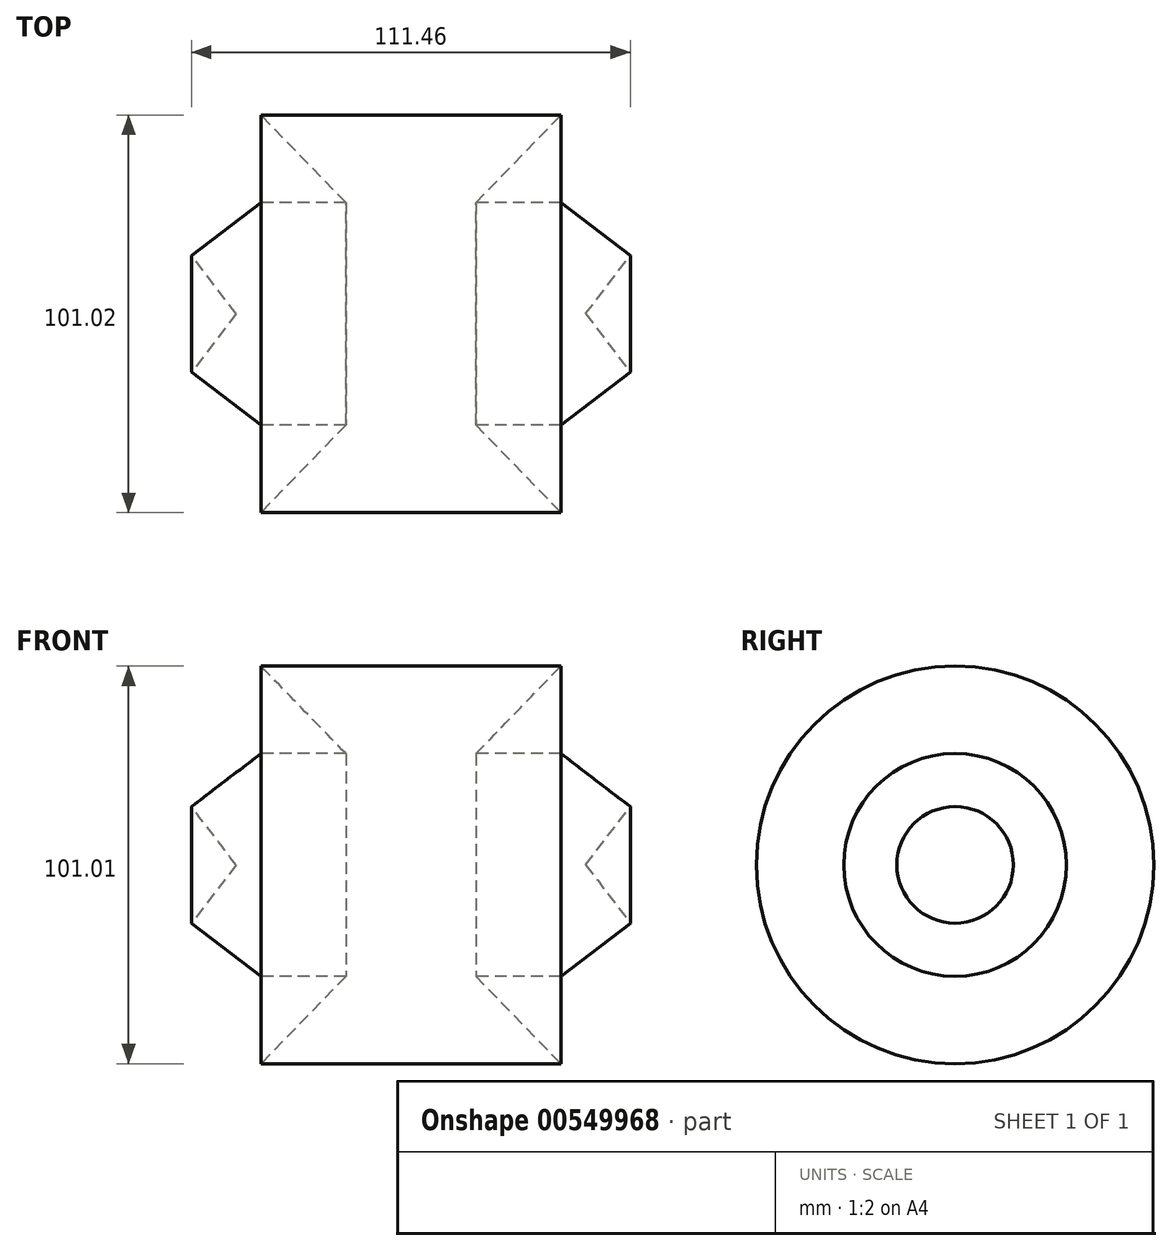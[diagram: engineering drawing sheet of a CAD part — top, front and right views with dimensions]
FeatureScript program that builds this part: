
annotation { "Feature Type Name" : "Feature", "Feature Type Description" : "" }
export const myFeature = defineFeature(function(context is Context, id is Id, definition is map)
    precondition{}
    {
        {
            var Q0;
            Q0=qCreatedBy(makeId("Front.planeOp"),FACE);
            var sketch = newSketch(context, id + "F0", { "sketchPlane" : qUnion([Q0])});
            skLineSegment(sketch, "E0", {"start": v(0, 14.8) * mm, "end": v(-44.41, 14.8) * mm});
            skLineSegment(sketch, "E1", {"start": v(0, 14.8) * mm, "end": v(44.41, 14.8) * mm});
            skLineSegment(sketch, "E2", {"start": v(-44.41, 14.8) * mm, "end": v(-55.73, 0) * mm});
            skLineSegment(sketch, "E3", {"start": v(44.41, 14.8) * mm, "end": v(55.73, 0) * mm});
            skLineSegment(sketch, "E4", {"start": v(-55.73, 0) * mm, "end": v(-38.1, -13.48) * mm});
            skLineSegment(sketch, "E5", {"start": v(55.73, 0) * mm, "end": v(38.1, -13.48) * mm});
            skLineSegment(sketch, "E6", {"start": v(-38.1, -13.48) * mm, "end": v(-16.55, -13.48) * mm});
            skLineSegment(sketch, "E7", {"start": v(38.1, -13.48) * mm, "end": v(16.55, -13.48) * mm});
            skLineSegment(sketch, "E8", {"start": v(-16.55, -13.48) * mm, "end": v(-38.1, -35.7) * mm});
            skLineSegment(sketch, "E9", {"start": v(16.55, -13.48) * mm, "end": v(38.1, -35.7) * mm});
            skLineSegment(sketch, "E10", {"start": v(-38.1, -35.7) * mm, "end": v(0, -35.7) * mm});
            skLineSegment(sketch, "E11", {"start": v(38.1, -35.7) * mm, "end": v(0, -35.7) * mm});
            skSolve(sketch);
        }
        {
            var Q0;
            Q0=makeQuery(id+"F0.imprint","IMPRINT",FACE,{"disambiguationData":[TD([[makeQuery(id+"F0.imprint","IMPRINT",EDGE,{"derivedFrom":sQuery(id+"F0.wireOp",EDGE,"E0")}),1.0]])]});
            var Q1;
            Q1=sQuery(id+"F0.wireOp",EDGE,"E1");
            revolve(context, id + "F1", {"entities" : qUnion([Q0]), "axis" : qUnion([Q1]), "revolveType" : RevolveType.FULL});
        }
    });
